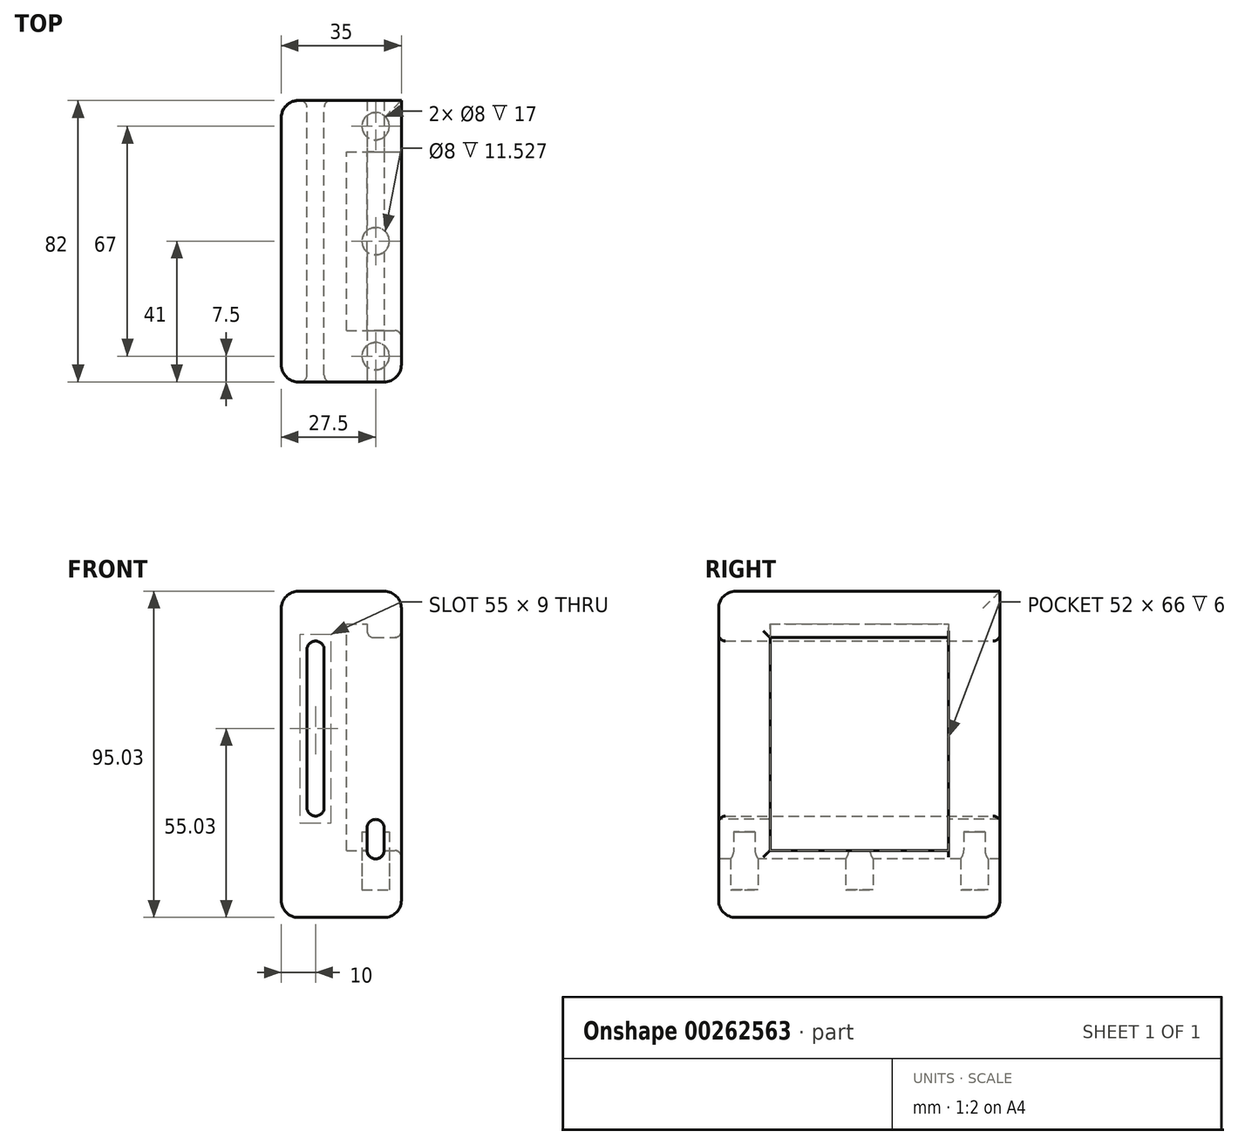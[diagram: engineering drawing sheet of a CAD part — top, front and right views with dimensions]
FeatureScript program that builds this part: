
annotation { "Feature Type Name" : "Feature", "Feature Type Description" : "" }
export const myFeature = defineFeature(function(context is Context, id is Id, definition is map)
    precondition{}
    {
        {
            var Q0;
            Q0=qCreatedBy(makeId("Front.planeOp"),FACE);
            var sketch = newSketch(context, id + "F0", { "sketchPlane" : qUnion([Q0])});
            skPoint(sketch, "E0.endSnap0", {"position": v(-18.75, 23) * mm});
            skArc(sketch, "E1", {"start": v(-17.5, 23) * mm, "mid": v(-20, 25.5) * mm, "end": v(-22.5, 23) * mm});
            skLineSegment(sketch, "E2", {"start": v(-17.5, 23) * mm, "end": v(-17.5, 0) * mm});
            skLineSegment(sketch, "E3", {"start": v(-22.5, 23) * mm, "end": v(-22.5, 0) * mm});
            skLineSegment(sketch, "E4.MirrorCS", {"start": v(-22.5, -23) * mm, "end": v(-22.5, 0) * mm});
            skArc(sketch, "E5.MirrorCS", {"start": v(-17.5, -23) * mm, "mid": v(-20, -25.5) * mm, "end": v(-22.5, -23) * mm});
            skLineSegment(sketch, "E6.MirrorCS", {"start": v(-17.5, -23) * mm, "end": v(-17.5, 0) * mm});
            skLineSegment(sketch, "E7.MirrorCS", {"start": v(-4.96, -47) * mm, "end": v(-4.96, -47.04) * mm});
            skLineSegment(sketch, "E8.trimOffspring", {"start": v(-4.96, -47.04) * mm, "end": v(-5, -47.04) * mm});
            skLineSegment(sketch, "E9", {"start": v(-11, 30.5) * mm, "end": v(-5, 30.5) * mm});
            skLineSegment(sketch, "E10", {"start": v(-5, 30.5) * mm, "end": v(-5, 26.5) * mm});
            skLineSegment(sketch, "E11", {"start": v(-30, 0) * mm, "end": v(-30, 40) * mm});
            skLineSegment(sketch, "E12", {"start": v(-30, 40) * mm, "end": v(5, 40) * mm});
            skLineSegment(sketch, "E13", {"start": v(-30, 0) * mm, "end": v(-11, 0) * mm});
            skLineSegment(sketch, "E14", {"start": v(-11, 0) * mm, "end": v(-11, 30.5) * mm});
            skLineSegment(sketch, "E15", {"start": v(-5, 26.5) * mm, "end": v(5, 26.5) * mm});
            skLineSegment(sketch, "E16", {"start": v(5, 26.5) * mm, "end": v(5, 40) * mm});
            skLineSegment(sketch, "E17", {"start": v(-11, 0) * mm, "end": v(-11, -30.5) * mm});
            skLineSegment(sketch, "E18", {"start": v(-11, -30.5) * mm, "end": v(-5, -30.5) * mm});
            skLineSegment(sketch, "E19", {"start": v(-5, -30.5) * mm, "end": v(-5, -26.5) * mm});
            skLineSegment(sketch, "E20", {"start": v(-5, -26.5) * mm, "end": v(5, -26.5) * mm});
            skLineSegment(sketch, "E21", {"start": v(5, -26.5) * mm, "end": v(5, -45.5) * mm});
            skLineSegment(sketch, "E22", {"start": v(-30, -45.03) * mm, "end": v(-30, 0) * mm});
            skLineSegment(sketch, "E23", {"start": v(-11, -30.5) * mm, "end": v(-11, -35.5) * mm});
            skLineSegment(sketch, "E24", {"start": v(-11, -35.5) * mm, "end": v(5, -35.5) * mm});
            skLineSegment(sketch, "E25", {"start": v(-30, -45.03) * mm, "end": v(-30, -55.03) * mm});
            skLineSegment(sketch, "E26", {"start": v(-30, -55.03) * mm, "end": v(5, -55.03) * mm});
            skLineSegment(sketch, "E27", {"start": v(5, -55.03) * mm, "end": v(5, -45.5) * mm});
            skLineSegment(sketch, "E28", {"start": v(-5, -30.5) * mm, "end": v(5, -30.5) * mm});
            skSolve(sketch);
        }
        {
            var Q0;
            Q0=makeQuery(id+"F0.imprint","IMPRINT",FACE,{"disambiguationData":[TD([[makeQuery(id+"F0.imprint","IMPRINT",EDGE,{"derivedFrom":sQuery(id+"F0.wireOp",EDGE,"E1")}),-1.0]])]});
            var Q1;
            {var subQ7=sQuery(id+"F0.wireOp",EDGE,"E4.MirrorCS");Q1=makeQuery(id+"F0.imprint","IMPRINT",FACE,{"disambiguationData":[TD([[makeQuery(id+"F0.imprint","IMPRINT",EDGE,{"derivedFrom":subQ7}),1.0]])]});}
            extrude(context, id + "F1", {"entities" : qUnion([Q0, Q1]), "endBound" : BoundingType.SYMMETRIC, "depth" : 52 * mm});
        }
        {
            var Q0;
            Q0=makeQuery(id+"F1.opExtrude","CAP_FACE",FACE,{"disambiguationData":[OSD([sQuery(id+"F0.wireOp",EDGE,"E1"),sQuery(id+"F0.wireOp",EDGE,"E2"),sQuery(id+"F0.wireOp",EDGE,"E3"),sQuery(id+"F0.wireOp",EDGE,"E4.MirrorCS"),sQuery(id+"F0.wireOp",EDGE,"E5.MirrorCS"),sQuery(id+"F0.wireOp",EDGE,"E6.MirrorCS"),sQuery(id+"F0.wireOp",EDGE,"E9"),sQuery(id+"F0.wireOp",EDGE,"E10"),sQuery(id+"F0.wireOp",EDGE,"E11"),sQuery(id+"F0.wireOp",EDGE,"E12"),sQuery(id+"F0.wireOp",EDGE,"E14"),sQuery(id+"F0.wireOp",EDGE,"E15"),sQuery(id+"F0.wireOp",EDGE,"E16"),sQuery(id+"F0.wireOp",EDGE,"E17"),sQuery(id+"F0.wireOp",EDGE,"E21"),sQuery(id+"F0.wireOp",EDGE,"ybgxOHrF-ffVe-eHHn-ETUF-HXYFG16J00Mp"),sQuery(id+"F0.wireOp",EDGE,"E22"),sQuery(id+"F0.wireOp",EDGE,"E23"),sQuery(id+"F0.wireOp",EDGE,"E24")])],"isStart":false});
            var sketch = newSketch(context, id + "F2", { "sketchPlane" : qUnion([Q0])});
            skLineSegment(sketch, "E29.bottom", {"start": v(-30, 40) * mm, "end": v(5, 40) * mm});
            skLineSegment(sketch, "E29.top", {"start": v(-30, -35.5) * mm, "end": v(5, -35.5) * mm});
            skLineSegment(sketch, "E29.left", {"start": v(-30, 40) * mm, "end": v(-30, -35.5) * mm});
            skLineSegment(sketch, "E29.right", {"start": v(5, 40) * mm, "end": v(5, -35.5) * mm});
            skArc(sketch, "E30", {"start": v(-17.5, 23) * mm, "mid": v(-20, 25.5) * mm, "end": v(-22.5, 23) * mm});
            skLineSegment(sketch, "E31", {"start": v(-17.5, 23) * mm, "end": v(-17.5, 0) * mm});
            skLineSegment(sketch, "E32", {"start": v(-22.5, 23) * mm, "end": v(-22.5, 0) * mm});
            skLineSegment(sketch, "E33.MirrorCS", {"start": v(-22.5, -23) * mm, "end": v(-22.5, 0) * mm});
            skArc(sketch, "E34.MirrorCS", {"start": v(-17.5, -23) * mm, "mid": v(-20, -25.5) * mm, "end": v(-22.5, -23) * mm});
            skLineSegment(sketch, "E35.MirrorCS", {"start": v(-17.5, -23) * mm, "end": v(-17.5, 0) * mm});
            skSolve(sketch);
        }
        {
            var Q0;
            Q0=qSketchRegion(id+"F2",true);
            var Q1;
            {var subQ1=makeQuery(id+"F1.opExtrude","CAP_EDGE",EDGE,{"disambiguationData":[OSD([sQuery(id+"F0.wireOp",EDGE,"E26")])],"isStart":false});Q1=makeQuery(id+"F2.imprint","IMPRINT",FACE,{"disambiguationData":[TD([[makeQuery(id+"F2.imprint","IMPRINT",EDGE,{"derivedFrom":subQ1}),1.0]])]});}
            extrude(context, id + "F3", {"entities" : qUnion([Q0, Q1]), "operationType" : NewBodyOperationType.ADD, "depth" : 15 * mm});
        }
        {
            var Q0;
            Q0=makeQuery(id+"F1.opExtrude","CAP_FACE",FACE,{"disambiguationData":[OSD([sQuery(id+"F0.wireOp",EDGE,"E1"),sQuery(id+"F0.wireOp",EDGE,"E2"),sQuery(id+"F0.wireOp",EDGE,"E3"),sQuery(id+"F0.wireOp",EDGE,"E4.MirrorCS"),sQuery(id+"F0.wireOp",EDGE,"E5.MirrorCS"),sQuery(id+"F0.wireOp",EDGE,"E6.MirrorCS"),sQuery(id+"F0.wireOp",EDGE,"E9"),sQuery(id+"F0.wireOp",EDGE,"E10"),sQuery(id+"F0.wireOp",EDGE,"E11"),sQuery(id+"F0.wireOp",EDGE,"E12"),sQuery(id+"F0.wireOp",EDGE,"E14"),sQuery(id+"F0.wireOp",EDGE,"E15"),sQuery(id+"F0.wireOp",EDGE,"E16"),sQuery(id+"F0.wireOp",EDGE,"E17"),sQuery(id+"F0.wireOp",EDGE,"E21"),sQuery(id+"F0.wireOp",EDGE,"E22"),sQuery(id+"F0.wireOp",EDGE,"E23"),sQuery(id+"F0.wireOp",EDGE,"E24"),sQuery(id+"F0.wireOp",EDGE,"E25"),sQuery(id+"F0.wireOp",EDGE,"E26"),sQuery(id+"F0.wireOp",EDGE,"E27")])],"isStart":true});
            var sketch = newSketch(context, id + "F4", { "sketchPlane" : qUnion([Q0])});
            skLineSegment(sketch, "E36.bottom", {"start": v(-5, 40) * mm, "end": v(30, 40) * mm});
            skLineSegment(sketch, "E36.top", {"start": v(-5, -55.03) * mm, "end": v(30, -55.03) * mm});
            skLineSegment(sketch, "E36.left", {"start": v(-5, 40) * mm, "end": v(-5, -55.03) * mm});
            skLineSegment(sketch, "E36.right", {"start": v(30, 40) * mm, "end": v(30, -55.03) * mm});
            skArc(sketch, "E37", {"start": v(22.5, 23) * mm, "mid": v(20, 25.5) * mm, "end": v(17.5, 23) * mm});
            skLineSegment(sketch, "E38", {"start": v(22.5, 23) * mm, "end": v(22.5, 0) * mm});
            skLineSegment(sketch, "E39", {"start": v(17.5, 23) * mm, "end": v(17.5, 0) * mm});
            skLineSegment(sketch, "E40.MirrorCS", {"start": v(17.5, -23) * mm, "end": v(17.5, 0) * mm});
            skArc(sketch, "E41.MirrorCS", {"start": v(22.5, -23) * mm, "mid": v(20, -25.5) * mm, "end": v(17.5, -23) * mm});
            skLineSegment(sketch, "E42.MirrorCS", {"start": v(22.5, -23) * mm, "end": v(22.5, 0) * mm});
            skLineSegment(sketch, "E43", {"start": v(-5, -55.03) * mm, "end": v(-5, 40) * mm});
            skLineSegment(sketch, "E44", {"start": v(30, 40) * mm, "end": v(-5, 40) * mm});
            skSolve(sketch);
        }
        {
            var Q0;
            Q0=qSketchRegion(id+"F4",true);
            extrude(context, id + "F5", {"entities" : qUnion([Q0]), "operationType" : NewBodyOperationType.ADD, "depth" : 15 * mm});
        }
        {
            var Q0;
            Q0=qCreatedBy(makeId("Front.planeOp"),FACE);
            var sketch = newSketch(context, id + "F6", { "sketchPlane" : qUnion([Q0])});
            skLineSegment(sketch, "E45", {"start": v(0, -31.5) * mm, "end": v(-5, -31.5) * mm});
            skArc(sketch, "E46", {"start": v(0, -28.96) * mm, "mid": v(-2.5, -26.46) * mm, "end": v(-5, -28.96) * mm});
            skArc(sketch, "E47", {"start": v(-5, -35.46) * mm, "mid": v(-2.5, -37.96) * mm, "end": v(0, -35.46) * mm});
            skLineSegment(sketch, "E48", {"start": v(-5, -28.96) * mm, "end": v(-5, -35.46) * mm});
            skLineSegment(sketch, "E49", {"start": v(0, -28.96) * mm, "end": v(0, -35.46) * mm});
            skSolve(sketch);
        }
        {
            var Q0;
            Q0=qSketchRegion(id+"F6",true);
            extrude(context, id + "F7", {"entities" : qUnion([Q0]), "operationType" : NewBodyOperationType.REMOVE, "endBound" : BoundingType.SYMMETRIC, "oppositeDirection" : true, "depth" : 100 * mm});
        }
        {
            var Q0;
            {var subQ0=sQuery(id+"F0.wireOp",EDGE,"E26");Q0=makeQuery(id+"F5.boolean.opBoolean","MERGE",FACE,{"derivedFrom":[makeQuery(id+"F3.boolean.opBoolean","MERGE",FACE,{"derivedFrom":[makeQuery(id+"F1.opExtrude","SWEPT_FACE",FACE,{"disambiguationData":[OSD([subQ0])]}),makeQuery(id+"F3.opExtrude","SWEPT_FACE",FACE,{"disambiguationData":[OSD([subQ0])]})]}),makeQuery(id+"F5.opExtrude","SWEPT_FACE",FACE,{"disambiguationData":[OSD([sQuery(id+"F4.wireOp",EDGE,"E36.top")])]})]});}
            var sketch = newSketch(context, id + "F8", { "sketchPlane" : qUnion([Q0])});
            skLineSegment(sketch, "E50", {"start": v(0, 0) * mm, "end": v(0, -41) * mm});
            skLineSegment(sketch, "E51", {"start": v(0, -41) * mm, "end": v(0, -36) * mm});
            skLineSegment(sketch, "E52", {"start": v(0, -36) * mm, "end": v(-2.5, -36) * mm});
            skCircle(sketch, "E53", {"center": v(-2.5, -33.5) * mm, "radius": 4 * mm});
            skLineSegment(sketch, "E54", {"start": v(0, 41) * mm, "end": v(0, 36) * mm});
            skLineSegment(sketch, "E55", {"start": v(0, 36) * mm, "end": v(-2.5, 36) * mm});
            skCircle(sketch, "E56", {"center": v(-2.5, 33.5) * mm, "radius": 4 * mm});
            skLineSegment(sketch, "E57", {"start": v(0, 0) * mm, "end": v(-2.5, 0) * mm});
            skCircle(sketch, "E58", {"center": v(-2.5, 0) * mm, "radius": 4 * mm});
            skSolve(sketch);
        }
        {
            var Q0;
            Q0=makeQuery(id+"F7.boolean.opBoolean","SPLIT",FACE,{"disambiguationData":[TD([makeQuery(id+"F1.opExtrude","SWEPT_FACE",FACE,{"disambiguationData":[OSD([sQuery(id+"F0.wireOp",EDGE,"E14"),sQuery(id+"F0.wireOp",EDGE,"E17"),sQuery(id+"F0.wireOp",EDGE,"E23")])]})])],"derivedFrom":makeQuery(id+"F1.opExtrude","SWEPT_FACE",FACE,{"disambiguationData":[OSD([sQuery(id+"F0.wireOp",EDGE,"E24")])]})});
            var sketch = newSketch(context, id + "F9", { "sketchPlane" : qUnion([Q0])});
            skLineSegment(sketch, "E59", {"start": v(-2.5, 0) * mm, "end": v(-2.5, -33.5) * mm});
            skLineSegment(sketch, "E60", {"start": v(-2.5, 0) * mm, "end": v(-2.5, 33.5) * mm});
            skCircle(sketch, "E61", {"center": v(-2.5, 33.5) * mm, "radius": 4 * mm});
            skCircle(sketch, "E62", {"center": v(-2.5, 0) * mm, "radius": 4 * mm});
            skCircle(sketch, "E63", {"center": v(-2.5, -33.5) * mm, "radius": 4 * mm});
            skSolve(sketch);
        }
        {
            var Q0;
            Q0=makeQuery(id+"F8.imprint","IMPRINT",FACE,{"disambiguationData":[TD([[makeQuery(id+"F8.imprint","IMPRINT",EDGE,{"derivedFrom":sQuery(id+"F8.wireOp",EDGE,"E58")}),1.0]])]});
            var Q1;
            {var subQ0=sQuery(id+"F8.wireOp",EDGE,"E51");var subQ1=sQuery(id+"F8.wireOp",EDGE,"E50");var subQ2=makeQuery(id+"F8.imprint","INTERSECT",VERTEX,{"derivedFrom":[subQ1,subQ0]});Q1=makeQuery(id+"F8.imprint","IMPRINT",FACE,{"disambiguationData":[TD([[makeQuery(id+"F8.imprint","IMPRINT",EDGE,{"disambiguationData":[TD([[subQ2,1.0]])],"derivedFrom":subQ1}),1.0]])]});}
            var Q2;
            {var subQ0=sQuery(id+"F8.wireOp",EDGE,"E51");var subQ1=sQuery(id+"F8.wireOp",EDGE,"E50");var subQ2=makeQuery(id+"F8.imprint","INTERSECT",VERTEX,{"derivedFrom":[subQ1,subQ0]});Q2=makeQuery(id+"F8.imprint","IMPRINT",FACE,{"disambiguationData":[TD([[makeQuery(id+"F8.imprint","IMPRINT",EDGE,{"disambiguationData":[TD([[subQ2,1.0]])],"derivedFrom":subQ1}),-1.0]])]});}
            var Q3;
            Q3=makeQuery(id+"F8.imprint","IMPRINT",FACE,{"disambiguationData":[TD([[makeQuery(id+"F8.imprint","IMPRINT",EDGE,{"derivedFrom":sQuery(id+"F8.wireOp",EDGE,"E56")}),1.0]])]});
            extrude(context, id + "F10", {"entities" : qUnion([Q0, Q1, Q2, Q3]), "operationType" : NewBodyOperationType.REMOVE, "oppositeDirection" : true, "depth" : 25 * mm, "hasSecondDirection" : true, "secondDirectionOppositeDirection" : true, "secondDirectionDepth" : 8 * mm});
        }
        {
            var Q0;
            Q0=makeQuery(id+"F3.opExtrude","CAP_EDGE",EDGE,{"disambiguationData":[OSD([sQuery(id+"F2.wireOp",EDGE,"E29.bottom")])],"isStart":false});
            var Q1;
            Q1=makeQuery(id+"F5.opExtrude","CAP_EDGE",EDGE,{"disambiguationData":[OSD([sQuery(id+"F4.wireOp",EDGE,"E44")])],"isStart":false});
            var Q2;
            Q2=makeQuery(id+"F5.opExtrude","CAP_EDGE",EDGE,{"disambiguationData":[OSD([sQuery(id+"F4.wireOp",EDGE,"E36.top")])],"isStart":false});
            var Q3;
            Q3=makeQuery(id+"F3.opExtrude","CAP_EDGE",EDGE,{"disambiguationData":[OSD([sQuery(id+"F0.wireOp",EDGE,"E26")])],"isStart":false});
            var Q4;
            Q4=makeQuery(id+"F3.opExtrude","CAP_EDGE",EDGE,{"disambiguationData":[OSD([sQuery(id+"F0.wireOp",EDGE,"E21"),sQuery(id+"F0.wireOp",EDGE,"E27"),sQuery(id+"F2.wireOp",EDGE,"E29.right")])],"isStart":false});
            var Q5;
            Q5=makeQuery(id+"F5.opExtrude","CAP_EDGE",EDGE,{"disambiguationData":[OSD([sQuery(id+"F4.wireOp",EDGE,"E43")])],"isStart":false});
            var Q6;
            Q6=makeQuery(id+"F5.boolean.opBoolean","MERGE",EDGE,{"derivedFrom":[makeQuery(id+"F3.boolean.opBoolean","MERGE",EDGE,{"derivedFrom":[makeQuery(id+"F1.opExtrude","SWEPT_EDGE",EDGE,{"disambiguationData":[OSD([sQuery(id+"F0.wireOp",EDGE,"E12"),sQuery(id+"F0.wireOp",EDGE,"E16")])]}),makeQuery(id+"F3.opExtrude","SWEPT_EDGE",EDGE,{"disambiguationData":[OSD([sQuery(id+"F2.wireOp",EDGE,"E29.bottom"),sQuery(id+"F2.wireOp",EDGE,"E29.right")])]})]}),makeQuery(id+"F5.opExtrude","SWEPT_EDGE",EDGE,{"disambiguationData":[OSD([sQuery(id+"F4.wireOp",EDGE,"E43"),sQuery(id+"F4.wireOp",EDGE,"E44")])]})]});
            var Q7;
            Q7=makeQuery(id+"F5.boolean.opBoolean","MERGE",EDGE,{"derivedFrom":[makeQuery(id+"F3.boolean.opBoolean","MERGE",EDGE,{"derivedFrom":[makeQuery(id+"F1.opExtrude","SWEPT_EDGE",EDGE,{"disambiguationData":[OSD([sQuery(id+"F0.wireOp",EDGE,"E11"),sQuery(id+"F0.wireOp",EDGE,"E12")])]}),makeQuery(id+"F3.opExtrude","SWEPT_EDGE",EDGE,{"disambiguationData":[OSD([sQuery(id+"F2.wireOp",EDGE,"E29.bottom"),sQuery(id+"F2.wireOp",EDGE,"E29.left")])]})]}),makeQuery(id+"F5.opExtrude","SWEPT_EDGE",EDGE,{"disambiguationData":[OSD([sQuery(id+"F4.wireOp",EDGE,"E36.right"),sQuery(id+"F4.wireOp",EDGE,"E44")])]})]});
            var Q8;
            Q8=makeQuery(id+"F3.opExtrude","CAP_EDGE",EDGE,{"disambiguationData":[OSD([sQuery(id+"F0.wireOp",EDGE,"E11"),sQuery(id+"F0.wireOp",EDGE,"E22"),sQuery(id+"F0.wireOp",EDGE,"E25"),sQuery(id+"F2.wireOp",EDGE,"E29.left")])],"isStart":false});
            var Q9;
            {var subQ0=sQuery(id+"F0.wireOp",EDGE,"E26");var subQ1=sQuery(id+"F0.wireOp",EDGE,"E25");Q9=makeQuery(id+"F5.boolean.opBoolean","MERGE",EDGE,{"derivedFrom":[makeQuery(id+"F3.boolean.opBoolean","MERGE",EDGE,{"derivedFrom":[makeQuery(id+"F1.opExtrude","SWEPT_EDGE",EDGE,{"disambiguationData":[OSD([subQ1,subQ0])]}),makeQuery(id+"F3.opExtrude","SWEPT_EDGE",EDGE,{"disambiguationData":[OSD([sQuery(id+"F0.wireOp",EDGE,"E11"),sQuery(id+"F0.wireOp",EDGE,"E22"),subQ1,subQ0])]})]}),makeQuery(id+"F5.opExtrude","SWEPT_EDGE",EDGE,{"disambiguationData":[OSD([sQuery(id+"F4.wireOp",EDGE,"E36.top"),sQuery(id+"F4.wireOp",EDGE,"E36.right")])]})]});}
            var Q10;
            Q10=makeQuery(id+"F5.opExtrude","CAP_EDGE",EDGE,{"disambiguationData":[OSD([sQuery(id+"F4.wireOp",EDGE,"E36.right")])],"isStart":false});
            var Q11;
            {var subQ0=sQuery(id+"F0.wireOp",EDGE,"E27");var subQ1=sQuery(id+"F0.wireOp",EDGE,"E26");Q11=makeQuery(id+"F5.boolean.opBoolean","MERGE",EDGE,{"derivedFrom":[makeQuery(id+"F3.boolean.opBoolean","MERGE",EDGE,{"derivedFrom":[makeQuery(id+"F1.opExtrude","SWEPT_EDGE",EDGE,{"disambiguationData":[OSD([subQ1,subQ0])]}),makeQuery(id+"F3.opExtrude","SWEPT_EDGE",EDGE,{"disambiguationData":[OSD([sQuery(id+"F0.wireOp",EDGE,"E21"),subQ1,subQ0])]})]}),makeQuery(id+"F5.opExtrude","SWEPT_EDGE",EDGE,{"disambiguationData":[OSD([sQuery(id+"F4.wireOp",EDGE,"E36.top"),sQuery(id+"F4.wireOp",EDGE,"E43")])]})]});}
            fillet(context, id + "F11", {"entities" : qUnion([Q0, Q1, Q2, Q3, Q4, Q5, Q6, Q7, Q8, Q9, Q10, Q11]), "radius" : 5 * mm, "tangentPropagation" : true, "allowEdgeOverflow" : false});
        }
        {
            var Q0;
            Q0=makeQuery(id+"F3.opExtrude","CAP_EDGE",EDGE,{"disambiguationData":[OSD([sQuery(id+"F0.wireOp",EDGE,"E21"),sQuery(id+"F0.wireOp",EDGE,"E27"),sQuery(id+"F2.wireOp",EDGE,"E29.right")])],"isStart":true});
            var Q1;
            Q1=makeQuery(id+"F1.opExtrude","SWEPT_EDGE",EDGE,{"disambiguationData":[OSD([sQuery(id+"F0.wireOp",EDGE,"E21"),sQuery(id+"F0.wireOp",EDGE,"E24")])]});
            var Q2;
            Q2=makeQuery(id+"F5.opExtrude","CAP_EDGE",EDGE,{"disambiguationData":[OSD([sQuery(id+"F4.wireOp",EDGE,"E43")])],"isStart":true});
            var Q3;
            Q3=makeQuery(id+"F1.opExtrude","SWEPT_EDGE",EDGE,{"disambiguationData":[OSD([sQuery(id+"F0.wireOp",EDGE,"E15"),sQuery(id+"F0.wireOp",EDGE,"E16")])]});
            var Q4;
            Q4=makeQuery(id+"F1.opExtrude","SWEPT_EDGE",EDGE,{"disambiguationData":[OSD([sQuery(id+"F0.wireOp",EDGE,"E10"),sQuery(id+"F0.wireOp",EDGE,"E15")])]});
            var Q5;
            {var subQ0=makeQuery(id+"F1.opExtrude","SWEPT_FACE",FACE,{"disambiguationData":[OSD([sQuery(id+"F0.wireOp",EDGE,"E24")])]});var subQ1=makeQuery(id+"F7.opExtrude","SWEPT_FACE",FACE,{"disambiguationData":[OSD([sQuery(id+"F6.wireOp",EDGE,"t2omA0GJ-bQSw-iscb-4RpO-IutBZPtcCuMd")])]});Q5=makeQuery(id+"FrNyJdjC94iPWeg_1.boolean.opBoolean","SPLIT",EDGE,{"disambiguationData":[TD([makeQuery(id+"F5.opExtrude","CAP_FACE",FACE,{"disambiguationData":[OSD([sQuery(id+"F4.wireOp",EDGE,"E36.top"),sQuery(id+"F4.wireOp",EDGE,"E36.right"),sQuery(id+"F4.wireOp",EDGE,"E37"),sQuery(id+"F4.wireOp",EDGE,"E38"),sQuery(id+"F4.wireOp",EDGE,"E39"),sQuery(id+"F4.wireOp",EDGE,"E40.MirrorCS"),sQuery(id+"F4.wireOp",EDGE,"E41.MirrorCS"),sQuery(id+"F4.wireOp",EDGE,"E42.MirrorCS"),sQuery(id+"F4.wireOp",EDGE,"E43"),sQuery(id+"F4.wireOp",EDGE,"E44")])],"isStart":true})])],"derivedFrom":makeQuery(id+"F7.boolean.opBoolean","INTERSECT",EDGE,{"derivedFrom":[subQ0,subQ1]})});}
            var Q6;
            {var subQ0=makeQuery(id+"F1.opExtrude","SWEPT_FACE",FACE,{"disambiguationData":[OSD([sQuery(id+"F0.wireOp",EDGE,"E24")])]});var subQ1=makeQuery(id+"F7.opExtrude","SWEPT_FACE",FACE,{"disambiguationData":[OSD([sQuery(id+"F6.wireOp",EDGE,"t2omA0GJ-bQSw-iscb-4RpO-IutBZPtcCuMd")])]});Q6=makeQuery(id+"FrNyJdjC94iPWeg_1.boolean.opBoolean","SPLIT",EDGE,{"disambiguationData":[TD([makeQuery(id+"F3.opExtrude","CAP_FACE",FACE,{"disambiguationData":[OSD([sQuery(id+"F0.wireOp",EDGE,"E11"),sQuery(id+"F0.wireOp",EDGE,"E21"),sQuery(id+"F0.wireOp",EDGE,"E22"),sQuery(id+"F0.wireOp",EDGE,"E25"),sQuery(id+"F0.wireOp",EDGE,"E26"),sQuery(id+"F0.wireOp",EDGE,"E27"),sQuery(id+"F2.wireOp",EDGE,"E29.bottom"),sQuery(id+"F2.wireOp",EDGE,"E29.left"),sQuery(id+"F2.wireOp",EDGE,"E29.right"),sQuery(id+"F2.wireOp",EDGE,"E30"),sQuery(id+"F2.wireOp",EDGE,"E31"),sQuery(id+"F2.wireOp",EDGE,"E32"),sQuery(id+"F2.wireOp",EDGE,"E33.MirrorCS"),sQuery(id+"F2.wireOp",EDGE,"E34.MirrorCS"),sQuery(id+"F2.wireOp",EDGE,"E35.MirrorCS")])],"isStart":true})])],"derivedFrom":makeQuery(id+"F7.boolean.opBoolean","INTERSECT",EDGE,{"derivedFrom":[subQ0,subQ1]})});}
            var Q7;
            {var subQ0=makeQuery(id+"F1.opExtrude","SWEPT_FACE",FACE,{"disambiguationData":[OSD([sQuery(id+"F0.wireOp",EDGE,"E24")])]});var subQ1=makeQuery(id+"F7.opExtrude","SWEPT_FACE",FACE,{"disambiguationData":[OSD([sQuery(id+"F6.wireOp",EDGE,"INmGDPkP-vWju-944D-qMyg-245BjJtDYb8f")])]});Q7=makeQuery(id+"FrNyJdjC94iPWeg_1.boolean.opBoolean","SPLIT",EDGE,{"disambiguationData":[TD([makeQuery(id+"F3.opExtrude","CAP_FACE",FACE,{"disambiguationData":[OSD([sQuery(id+"F0.wireOp",EDGE,"E11"),sQuery(id+"F0.wireOp",EDGE,"E21"),sQuery(id+"F0.wireOp",EDGE,"E22"),sQuery(id+"F0.wireOp",EDGE,"E25"),sQuery(id+"F0.wireOp",EDGE,"E26"),sQuery(id+"F0.wireOp",EDGE,"E27"),sQuery(id+"F2.wireOp",EDGE,"E29.bottom"),sQuery(id+"F2.wireOp",EDGE,"E29.left"),sQuery(id+"F2.wireOp",EDGE,"E29.right"),sQuery(id+"F2.wireOp",EDGE,"E30"),sQuery(id+"F2.wireOp",EDGE,"E31"),sQuery(id+"F2.wireOp",EDGE,"E32"),sQuery(id+"F2.wireOp",EDGE,"E33.MirrorCS"),sQuery(id+"F2.wireOp",EDGE,"E34.MirrorCS"),sQuery(id+"F2.wireOp",EDGE,"E35.MirrorCS")])],"isStart":true})])],"derivedFrom":makeQuery(id+"F7.boolean.opBoolean","INTERSECT",EDGE,{"derivedFrom":[subQ0,subQ1]})});}
            var Q8;
            {var subQ0=makeQuery(id+"F1.opExtrude","SWEPT_FACE",FACE,{"disambiguationData":[OSD([sQuery(id+"F0.wireOp",EDGE,"E24")])]});var subQ1=makeQuery(id+"F7.opExtrude","SWEPT_FACE",FACE,{"disambiguationData":[OSD([sQuery(id+"F6.wireOp",EDGE,"INmGDPkP-vWju-944D-qMyg-245BjJtDYb8f")])]});Q8=makeQuery(id+"FrNyJdjC94iPWeg_1.boolean.opBoolean","SPLIT",EDGE,{"disambiguationData":[TD([makeQuery(id+"F5.opExtrude","CAP_FACE",FACE,{"disambiguationData":[OSD([sQuery(id+"F4.wireOp",EDGE,"E36.top"),sQuery(id+"F4.wireOp",EDGE,"E36.right"),sQuery(id+"F4.wireOp",EDGE,"E37"),sQuery(id+"F4.wireOp",EDGE,"E38"),sQuery(id+"F4.wireOp",EDGE,"E39"),sQuery(id+"F4.wireOp",EDGE,"E40.MirrorCS"),sQuery(id+"F4.wireOp",EDGE,"E41.MirrorCS"),sQuery(id+"F4.wireOp",EDGE,"E42.MirrorCS"),sQuery(id+"F4.wireOp",EDGE,"E43"),sQuery(id+"F4.wireOp",EDGE,"E44")])],"isStart":true})])],"derivedFrom":makeQuery(id+"F7.boolean.opBoolean","INTERSECT",EDGE,{"derivedFrom":[subQ0,subQ1]})});}
            var Q9;
            Q9=makeQuery(id+"F3.opExtrude","CAP_EDGE",EDGE,{"disambiguationData":[OSD([sQuery(id+"F2.wireOp",EDGE,"E30")])],"isStart":false});
            var Q10;
            Q10=makeQuery(id+"F5.opExtrude","CAP_EDGE",EDGE,{"disambiguationData":[OSD([sQuery(id+"F4.wireOp",EDGE,"E39"),sQuery(id+"F4.wireOp",EDGE,"E40.MirrorCS")])],"isStart":false});
            fillet(context, id + "F12", {"entities" : qUnion([Q0, Q1, Q2, Q3, Q4, Q5, Q6, Q7, Q8, Q9, Q10]), "radius" : 2 * mm, "tangentPropagation" : true, "allowEdgeOverflow" : false});
        }
    });
